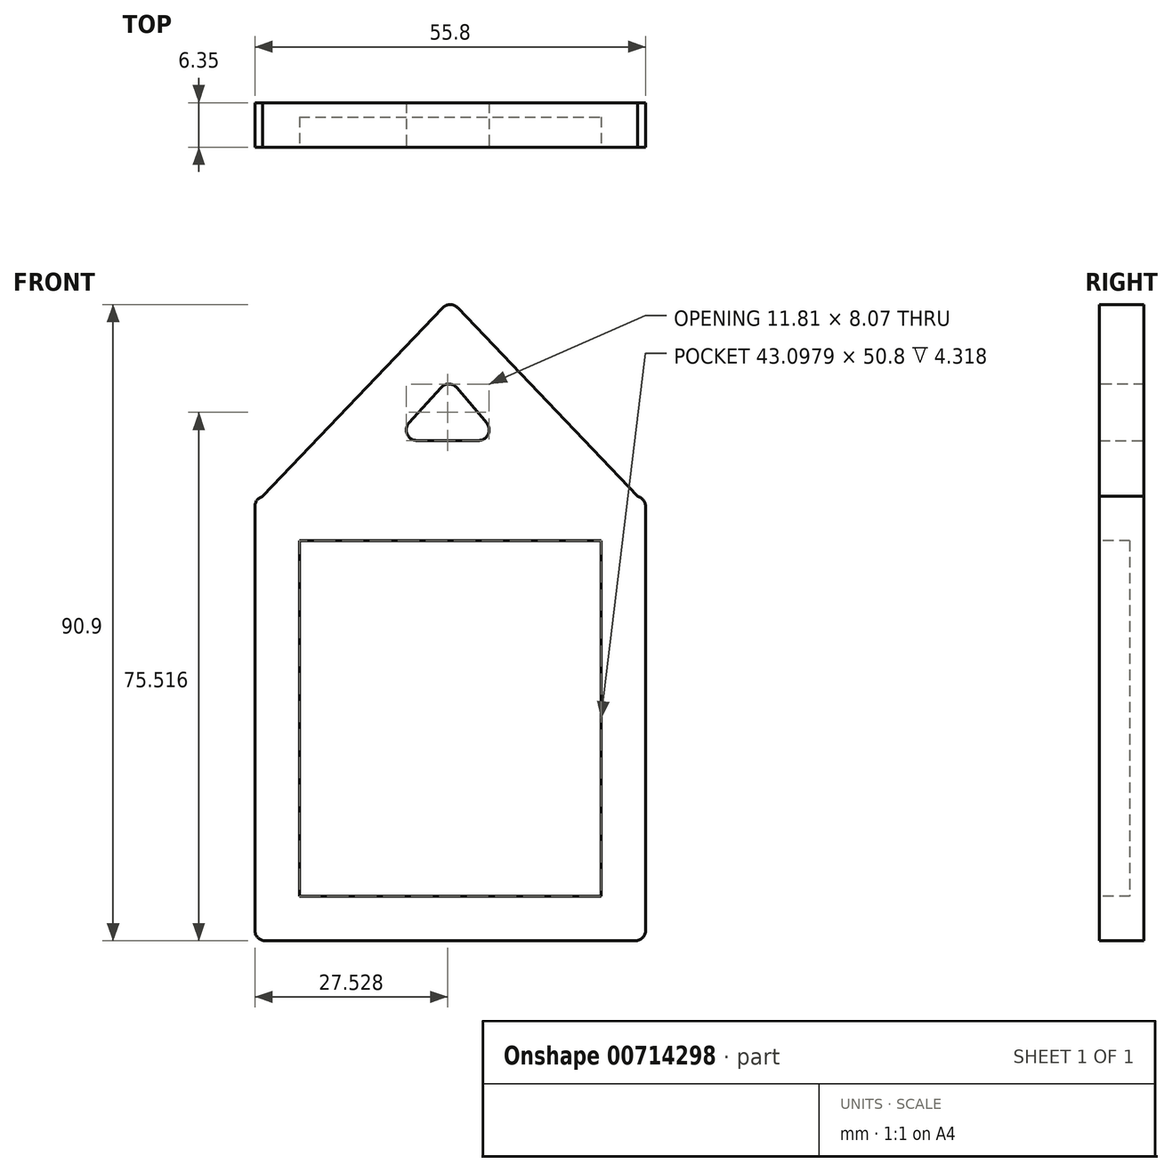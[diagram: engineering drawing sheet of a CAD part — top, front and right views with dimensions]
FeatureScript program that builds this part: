
annotation { "Feature Type Name" : "Feature", "Feature Type Description" : "" }
export const myFeature = defineFeature(function(context is Context, id is Id, definition is map)
    precondition{}
    {
        {
            var Q0;
            Q0=qCreatedBy(makeId("Front.planeOp"),FACE);
            var sketch = newSketch(context, id + "F0", { "sketchPlane" : qUnion([Q0])});
            skLineSegment(sketch, "E0", {"start": v(-40.6, 20.01) * mm, "end": v(-40.6, -19.3) * mm});
            skLineSegment(sketch, "E1", {"start": v(-40.6, -19.3) * mm, "end": v(-40.6, 20.01) * mm});
            skLineSegment(sketch, "E2", {"start": v(15.2, 20.01) * mm, "end": v(15.2, -19.3) * mm});
            skLineSegment(sketch, "E3", {"start": v(15.2, -19.3) * mm, "end": v(15.2, 20.01) * mm});
            skLineSegment(sketch, "E4", {"start": v(-40.6, -19.3) * mm, "end": v(-31.99, -19.3) * mm});
            skLineSegment(sketch, "E5", {"start": v(15.2, -19.3) * mm, "end": v(6.6, -19.3) * mm});
            skLineSegment(sketch, "E6", {"start": v(-40.6, 20.01) * mm, "end": v(-40.6, 44.2) * mm});
            skLineSegment(sketch, "E7", {"start": v(15.2, 20.01) * mm, "end": v(15.2, 44.2) * mm});
            skLineSegment(sketch, "E8", {"start": v(-31.99, -19.3) * mm, "end": v(6.6, -19.3) * mm});
            skLineSegment(sketch, "E9", {"start": v(-40.6, 44.2) * mm, "end": v(15.2, 44.2) * mm});
            skSolve(sketch);
        }
        {
            var Q0;
            Q0 = qSketchRegion(id + "F0", true);
            extrude(context, id + "F1", {"entities" : qUnion([Q0]), "depth" : 6.35 * mm, "offsetDistance" : 25.4 * mm});
        }
        {
            var Q0;
            Q0=makeQuery(id+"F1.opExtrude","CAP_FACE",FACE,{"disambiguationData":[OSD([sQuery(id+"F0.wireOp",EDGE,"E1"),sQuery(id+"F0.wireOp",EDGE,"E3"),sQuery(id+"F0.wireOp",EDGE,"E4"),sQuery(id+"F0.wireOp",EDGE,"E5"),sQuery(id+"F0.wireOp",EDGE,"E6"),sQuery(id+"F0.wireOp",EDGE,"E7"),sQuery(id+"F0.wireOp",EDGE,"E8"),sQuery(id+"F0.wireOp",EDGE,"E9")])],"isStart":false});
            var sketch = newSketch(context, id + "F2", { "sketchPlane" : qUnion([Q0])});
            skLineSegment(sketch, "E10.0", {"start": v(8.85, -12.95) * mm, "end": v(-34.25, -12.95) * mm});
            skLineSegment(sketch, "E10.1", {"start": v(8.85, -12.95) * mm, "end": v(8.85, 37.85) * mm});
            skLineSegment(sketch, "E10.2", {"start": v(-34.25, 37.85) * mm, "end": v(8.85, 37.85) * mm});
            skLineSegment(sketch, "E10.3", {"start": v(-34.25, -12.95) * mm, "end": v(-34.25, 37.85) * mm});
            skSolve(sketch);
        }
        {
            var Q0;
            Q0 = qSketchRegion(id + "F2", true);
            var Q1;
            Q1=makeQuery(id+"F1.opExtrude","CAP_FACE",FACE,{"disambiguationData":[OSD([sQuery(id+"F0.wireOp",EDGE,"E1"),sQuery(id+"F0.wireOp",EDGE,"E3"),sQuery(id+"F0.wireOp",EDGE,"E4"),sQuery(id+"F0.wireOp",EDGE,"E5"),sQuery(id+"F0.wireOp",EDGE,"E6"),sQuery(id+"F0.wireOp",EDGE,"E7"),sQuery(id+"F0.wireOp",EDGE,"E8"),sQuery(id+"F0.wireOp",EDGE,"E9")])],"isStart":true});
            extrude(context, id + "F3", {"entities" : qUnion([Q0]), "operationType" : NewBodyOperationType.REMOVE, "endBound" : BoundingType.UP_TO_SURFACE, "oppositeDirection" : true, "depth" : 21.59 * mm, "endBoundEntityFace" : qUnion([Q1]), "hasOffset" : true, "offsetDistance" : 2.03 * mm});
        }
        {
            var Q0;
            Q0=qCreatedBy(makeId("Front.planeOp"),FACE);
            var sketch = newSketch(context, id + "F4", { "sketchPlane" : qUnion([Q0])});
            skLineSegment(sketch, "E11", {"start": v(-12.7, 44.2) * mm, "end": v(-12.7, 44.2) * mm});
            skLineSegment(sketch, "E12", {"start": v(-39.46, 44.2) * mm, "end": v(-12.7, 72.28) * mm});
            skLineSegment(sketch, "E13", {"start": v(-12.7, 72.28) * mm, "end": v(14.04, 44.2) * mm});
            skLineSegment(sketch, "E14", {"start": v(-39.46, 44.2) * mm, "end": v(14.04, 44.2) * mm});
            skSolve(sketch);
        }
        {
            var Q0;
            Q0 = qSketchRegion(id + "F4", true);
            var Q1;
            Q1=makeQuery(id+"F1.opExtrude","CAP_FACE",FACE,{"disambiguationData":[OSD([sQuery(id+"F0.wireOp",EDGE,"E1"),sQuery(id+"F0.wireOp",EDGE,"E3"),sQuery(id+"F0.wireOp",EDGE,"E4"),sQuery(id+"F0.wireOp",EDGE,"E5"),sQuery(id+"F0.wireOp",EDGE,"E6"),sQuery(id+"F0.wireOp",EDGE,"E7"),sQuery(id+"F0.wireOp",EDGE,"E8"),sQuery(id+"F0.wireOp",EDGE,"E9")])],"isStart":false});
            extrude(context, id + "F5", {"entities" : qUnion([Q0]), "operationType" : NewBodyOperationType.ADD, "endBound" : BoundingType.UP_TO_SURFACE, "depth" : 25.4 * mm, "endBoundEntityFace" : qUnion([Q1]), "offsetDistance" : 25.4 * mm});
        }
        {
            var Q0;
            Q0=qCreatedBy(makeId("Front.planeOp"),FACE);
            var sketch = newSketch(context, id + "F6", { "sketchPlane" : qUnion([Q0])});
            skLineSegment(sketch, "E15", {"start": v(-12.87, 61.04) * mm, "end": v(-20.9, 52.18) * mm});
            skLineSegment(sketch, "E16", {"start": v(-20.9, 52.18) * mm, "end": v(-12.87, 61.04) * mm});
            skLineSegment(sketch, "E17", {"start": v(-20.9, 52.18) * mm, "end": v(-5.4, 52.18) * mm});
            skLineSegment(sketch, "E18", {"start": v(-5.4, 52.18) * mm, "end": v(-12.87, 61.04) * mm});
            skSolve(sketch);
        }
        {
            var Q0;
            Q0 = qSketchRegion(id + "F6", true);
            extrude(context, id + "F7", {"entities" : qUnion([Q0]), "operationType" : NewBodyOperationType.REMOVE, "endBound" : BoundingType.THROUGH_ALL, "depth" : 52.32 * mm, "offsetDistance" : 25.4 * mm});
        }
        {
            var Q0;
            Q0=makeQuery(id+"F5.opExtrude","SWEPT_EDGE",EDGE,{"disambiguationData":[OSD([sQuery(id+"F4.wireOp",EDGE,"E12"),sQuery(id+"F4.wireOp",EDGE,"E13")])]});
            var Q1;
            Q1=makeQuery(id+"F1.opExtrude","SWEPT_EDGE",EDGE,{"disambiguationData":[OSD([sQuery(id+"F0.wireOp",EDGE,"E7"),sQuery(id+"F0.wireOp",EDGE,"E9")])]});
            var Q2;
            Q2=makeQuery(id+"F7.boolean.opBoolean","COPY",EDGE,{"derivedFrom":makeQuery(id+"F7.opExtrude","SWEPT_EDGE",EDGE,{"disambiguationData":[OSD([sQuery(id+"F6.wireOp",EDGE,"E16"),sQuery(id+"F6.wireOp",EDGE,"E17")])]})});
            var Q3;
            Q3=makeQuery(id+"F1.opExtrude","SWEPT_EDGE",EDGE,{"disambiguationData":[OSD([sQuery(id+"F0.wireOp",EDGE,"E6"),sQuery(id+"F0.wireOp",EDGE,"E9")])]});
            var Q4;
            Q4=makeQuery(id+"F7.boolean.opBoolean","COPY",EDGE,{"derivedFrom":makeQuery(id+"F7.opExtrude","SWEPT_EDGE",EDGE,{"disambiguationData":[OSD([sQuery(id+"F6.wireOp",EDGE,"E16"),sQuery(id+"F6.wireOp",EDGE,"E18")])]})});
            var Q5;
            Q5=makeQuery(id+"F7.boolean.opBoolean","COPY",EDGE,{"derivedFrom":makeQuery(id+"F7.opExtrude","SWEPT_EDGE",EDGE,{"disambiguationData":[OSD([sQuery(id+"F6.wireOp",EDGE,"E17"),sQuery(id+"F6.wireOp",EDGE,"E18")])]})});
            var Q6;
            Q6=makeQuery(id+"F1.opExtrude","SWEPT_EDGE",EDGE,{"disambiguationData":[OSD([sQuery(id+"F0.wireOp",EDGE,"E1"),sQuery(id+"F0.wireOp",EDGE,"E4")])]});
            var Q7;
            Q7=makeQuery(id+"F1.opExtrude","SWEPT_EDGE",EDGE,{"disambiguationData":[OSD([sQuery(id+"F0.wireOp",EDGE,"E3"),sQuery(id+"F0.wireOp",EDGE,"E5")])]});
            fillet(context, id + "F8", {"entities" : qUnion([Q0, Q1, Q2, Q3, Q4, Q5, Q6, Q7]), "radius" : 1.52 * mm, "tangentPropagation" : true, "allowEdgeOverflow" : false});
        }
    });
